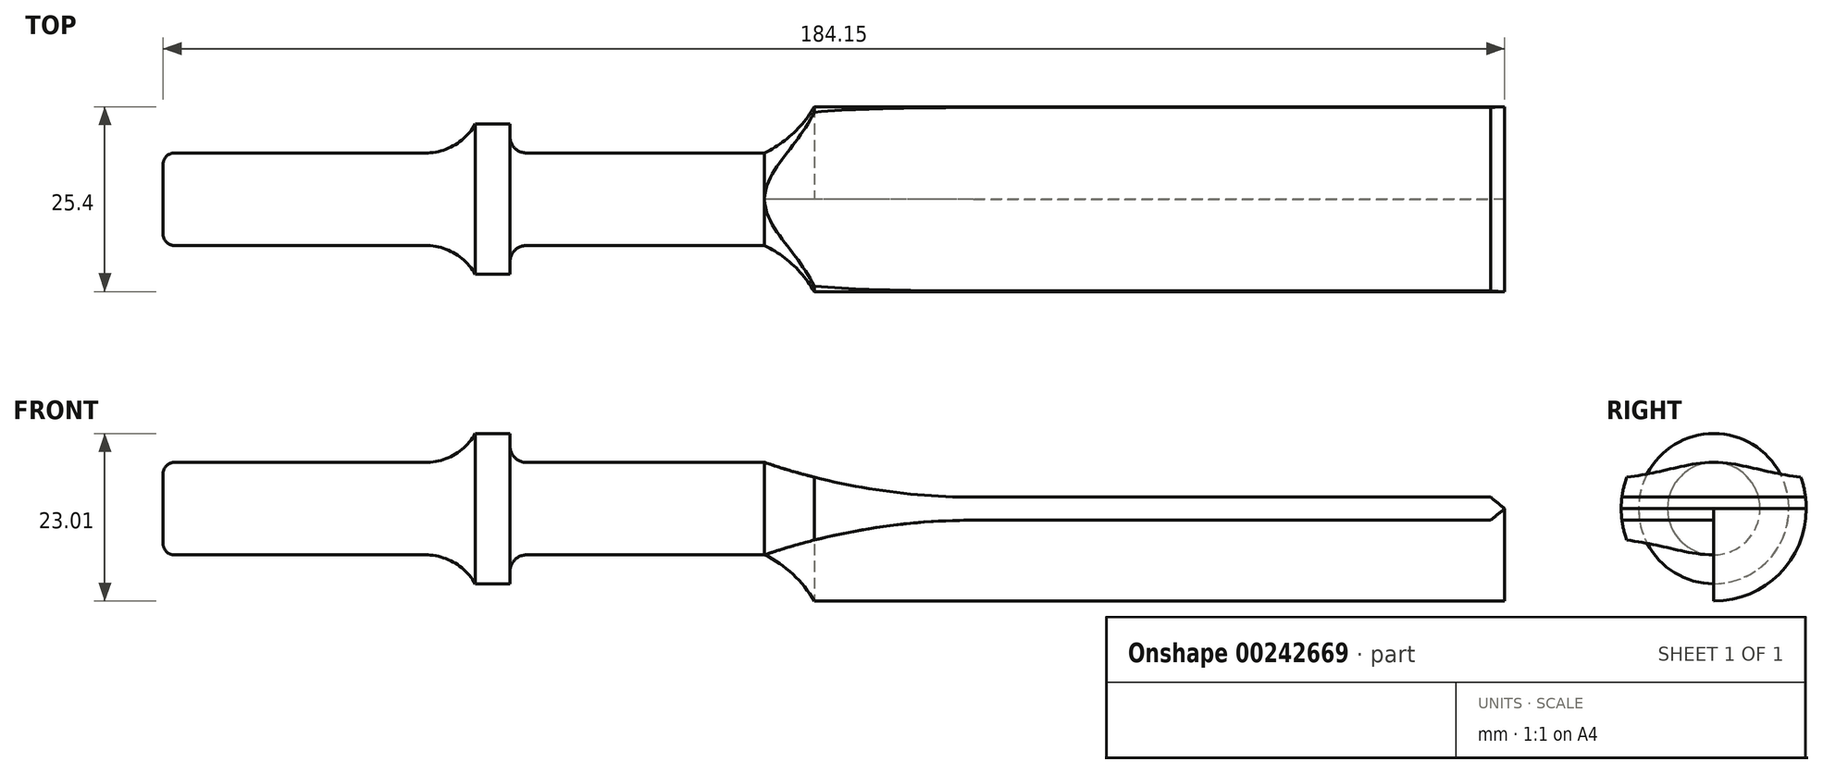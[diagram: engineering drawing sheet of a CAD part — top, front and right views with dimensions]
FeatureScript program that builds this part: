
annotation { "Feature Type Name" : "Feature", "Feature Type Description" : "" }
export const myFeature = defineFeature(function(context is Context, id is Id, definition is map)
    precondition{}
    {
        {
            var Q0;
            Q0=qCreatedBy(makeId("Front.planeOp"),FACE);
            var sketch = newSketch(context, id + "F0", { "sketchPlane" : qUnion([Q0])});
            skLineSegment(sketch, "E0", {"start": v(0, 0) * mm, "end": v(184.15, 0) * mm});
            skLineSegment(sketch, "E1", {"start": v(0, 0) * mm, "end": v(0, 4.83) * mm});
            skLineSegment(sketch, "E2", {"start": v(1.52, 6.35) * mm, "end": v(35.99, 6.35) * mm});
            skLineSegment(sketch, "E3", {"start": v(42.85, 10.31) * mm, "end": v(47.6, 10.31) * mm});
            skLineSegment(sketch, "E4", {"start": v(47.6, 10.31) * mm, "end": v(47.6, 8.64) * mm});
            skLineSegment(sketch, "E5", {"start": v(184.15, 0) * mm, "end": v(184.15, 12.7) * mm});
            skLineSegment(sketch, "E6.0", {"start": v(82.55, 0) * mm, "end": v(82.55, 12.7) * mm, "construction": true});
            skLineSegment(sketch, "E7.0", {"start": v(95.25, 0) * mm, "end": v(95.25, 12.7) * mm, "construction": true});
            skLineSegment(sketch, "E8", {"start": v(184.15, 12.7) * mm, "end": v(82.55, 12.7) * mm});
            skLineSegment(sketch, "E9.trimOffspring", {"start": v(49.89, 6.35) * mm, "end": v(95.25, 6.35) * mm});
            skArc(sketch, "E10", {"start": v(82.55, 6.35) * mm, "mid": v(86.44, 9.01) * mm, "end": v(89.38, 12.7) * mm});
            skLineSegment(sketch, "E11", {"start": v(75.63, 20.64) * mm, "end": v(75.63, 12.7) * mm});
            skPoint(sketch, "E12.orphan", {"position": v(75.63, 4.76) * mm});
            skPoint(sketch, "E13.end.orphan", {"position": v(80.92, 27.26) * mm});
            skPoint(sketch, "E14.end.orphan", {"position": v(80.92, 20.9) * mm});
            skPoint(sketch, "E15", {"position": v(82.55, 6.35) * mm});
            skArc(sketch, "E16", {"start": v(35.99, 6.35) * mm, "mid": v(39.95, 7.41) * mm, "end": v(42.85, 10.31) * mm});
            skPoint(sketch, "E17", {"position": v(42.85, 10.31) * mm});
            skPoint(sketch, "E18.orphan", {"position": v(47.6, 0) * mm});
            skPoint(sketch, "E19.visualSharp", {"position": v(0, 6.35) * mm});
            skArc(sketch, "E19.filletArc", {"start": v(1.52, 6.35) * mm, "mid": v(0.45, 5.9) * mm, "end": v(0, 4.83) * mm});
            skPoint(sketch, "E20.visualSharp", {"position": v(47.6, 6.35) * mm});
            skArc(sketch, "E20.filletArc", {"start": v(47.6, 8.64) * mm, "mid": v(48.27, 7.02) * mm, "end": v(49.89, 6.35) * mm});
            skSolve(sketch);
        }
        {
            var Q0;
            Q0=makeQuery(id+"F0.imprint","IMPRINT",FACE,{"disambiguationData":[TD([[makeQuery(id+"F0.imprint","IMPRINT",EDGE,{"derivedFrom":sQuery(id+"F0.wireOp",EDGE,"E0")}),1.0]])]});
            var Q1;
            Q1=sQuery(id+"F0.wireOp",EDGE,"E0");
            revolve(context, id + "F1", {"entities" : qUnion([Q0]), "axis" : qUnion([Q1]), "revolveType" : RevolveType.FULL});
        }
        {
            var Q0;
            Q0=qCreatedBy(makeId("Front.planeOp"),FACE);
            var sketch = newSketch(context, id + "F2", { "sketchPlane" : qUnion([Q0])});
            skLineSegment(sketch, "E21", {"start": v(0, 0) * mm, "end": v(184.15, 0) * mm, "construction": true});
            skLineSegment(sketch, "E22", {"start": v(184.15, 0) * mm, "end": v(184.15, 24.63) * mm, "construction": true});
            skLineSegment(sketch, "E23.0", {"start": v(82.55, 0) * mm, "end": v(82.55, 24.63) * mm, "construction": true});
            skLineSegment(sketch, "E24.0", {"start": v(0, 6.35) * mm, "end": v(184.15, 6.35) * mm, "construction": true});
            skLineSegment(sketch, "E25.0", {"start": v(82.55, 0) * mm, "end": v(184.15, 0) * mm, "construction": true});
            skPoint(sketch, "E26", {"position": v(82.55, 6.35) * mm});
            skArc(sketch, "E27", {"start": v(82.55, 6.35) * mm, "mid": v(96.7, 2.79) * mm, "end": v(111.26, 1.59) * mm});
            skLineSegment(sketch, "E28.trimOffspring", {"start": v(111.26, 1.59) * mm, "end": v(182.22, 1.59) * mm});
            skLineSegment(sketch, "E29", {"start": v(183.54, 6.35) * mm, "end": v(184.15, 0) * mm});
            skLineSegment(sketch, "E30.MirrorCS", {"start": v(184, -1.59) * mm, "end": v(184.15, 0) * mm});
            skArc(sketch, "E31.MirrorCS", {"start": v(82.55, -6.35) * mm, "mid": v(96.7, -2.79) * mm, "end": v(111.26, -1.59) * mm});
            skLineSegment(sketch, "E32.MirrorCS", {"start": v(111.26, -1.59) * mm, "end": v(182.22, -1.59) * mm});
            skPoint(sketch, "E33.end.orphan", {"position": v(171.9, 13.83) * mm});
            skPoint(sketch, "E34.MirrorCS.end.orphan", {"position": v(171.9, -13.83) * mm});
            skPoint(sketch, "E34.MirrorCS.start.orphan", {"position": v(184.15, -1.59) * mm});
            skPoint(sketch, "E35.start.orphan", {"position": v(0, 49.76) * mm});
            skPoint(sketch, "E36.MirrorCS.end.orphan", {"position": v(0, -49.76) * mm});
            skPoint(sketch, "E36.MirrorCS.start.orphan", {"position": v(0, -6.35) * mm});
            skPoint(sketch, "E37.MirrorCS.end.orphan", {"position": v(179.45, -48.56) * mm});
            skLineSegment(sketch, "E38", {"start": v(82.55, 6.35) * mm, "end": v(82.55, 49.72) * mm});
            skLineSegment(sketch, "E39.MirrorCS", {"start": v(82.55, -6.35) * mm, "end": v(82.55, -49.72) * mm});
            skPoint(sketch, "E40.end.orphan", {"position": v(178.03, 7.71) * mm});
            skPoint(sketch, "E41.MirrorCS.end.orphan", {"position": v(178.03, -7.71) * mm});
            skLineSegment(sketch, "E42", {"start": v(184.15, 0) * mm, "end": v(182.22, 1.59) * mm});
            skLineSegment(sketch, "E43.MirrorCS", {"start": v(184.15, 0) * mm, "end": v(182.22, -1.59) * mm});
            skLineSegment(sketch, "E44.trimOffspring", {"start": v(184, 1.59) * mm, "end": v(184.15, 1.59) * mm});
            skLineSegment(sketch, "E45.trimOffspring", {"start": v(184, -1.59) * mm, "end": v(184.15, -1.59) * mm});
            skPoint(sketch, "E46.end.orphan", {"position": v(179.45, 48.56) * mm});
            skPoint(sketch, "E47.MirrorCS.start.orphan", {"position": v(82.55, -49.72) * mm});
            skLineSegment(sketch, "E48", {"start": v(82.55, -49.72) * mm, "end": v(205.58, -48.56) * mm});
            skLineSegment(sketch, "E49", {"start": v(82.55, 49.72) * mm, "end": v(205.58, 50.88) * mm});
            skLineSegment(sketch, "E50", {"start": v(205.58, 50.88) * mm, "end": v(184.15, 0) * mm});
            skLineSegment(sketch, "E51.MirrorCS", {"start": v(205.58, -50.88) * mm, "end": v(184.15, 0) * mm});
            skSolve(sketch);
        }
        {
            var Q0;
            Q0=makeQuery(id+"F2.imprint","IMPRINT",FACE,{"disambiguationData":[TD([[makeQuery(id+"F2.imprint","IMPRINT",EDGE,{"derivedFrom":sQuery(id+"F2.wireOp",EDGE,"E27")}),1.0]])]});
            var Q1;
            Q1=makeQuery(id+"F2.imprint","IMPRINT",FACE,{"disambiguationData":[TD([[makeQuery(id+"F2.imprint","IMPRINT",EDGE,{"derivedFrom":sQuery(id+"F2.wireOp",EDGE,"E31.MirrorCS")}),-1.0]])]});
            extrude(context, id + "F3", {"entities" : qUnion([Q0, Q1]), "operationType" : NewBodyOperationType.REMOVE, "oppositeDirection" : true, "depth" : 25.4 * mm});
        }
        {
            var Q0;
            Q0 = qSketchRegion(id + "F2", true);
            extrude(context, id + "F4", {"entities" : qUnion([Q0]), "operationType" : NewBodyOperationType.REMOVE, "depth" : 25.4 * mm});
        }
    });
